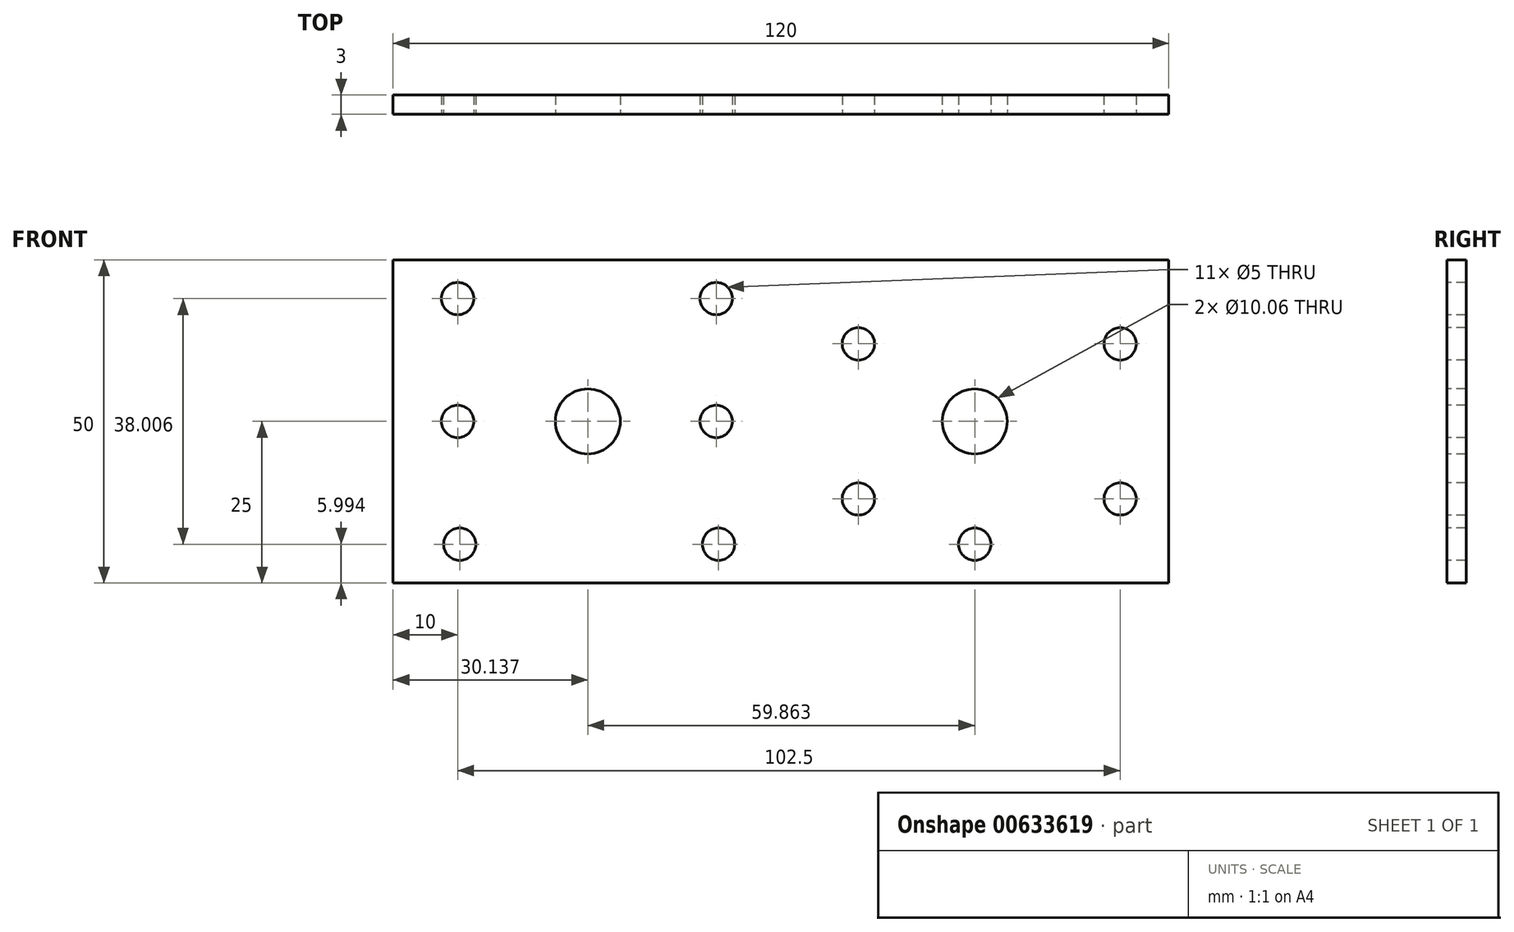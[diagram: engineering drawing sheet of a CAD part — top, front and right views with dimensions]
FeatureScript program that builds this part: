
annotation { "Feature Type Name" : "Feature", "Feature Type Description" : "" }
export const myFeature = defineFeature(function(context is Context, id is Id, definition is map)
    precondition{}
    {
        {
            var Q0;
            Q0=qCreatedBy(makeId("Front.planeOp"),FACE);
            var sketch = newSketch(context, id + "F0", { "sketchPlane" : qUnion([Q0])});
            skLineSegment(sketch, "E0.bottom", {"start": v(60, -25) * mm, "end": v(-60, -25) * mm});
            skLineSegment(sketch, "E0.top", {"start": v(60, 25) * mm, "end": v(-60, 25) * mm});
            skLineSegment(sketch, "E0.left", {"start": v(60, -25) * mm, "end": v(60, 25) * mm});
            skLineSegment(sketch, "E0.right", {"start": v(-60, -25) * mm, "end": v(-60, 25) * mm});
            skPoint(sketch, "E0.middle", {"position": v(0, 0) * mm});
            skSolve(sketch);
        }
        {
            var Q0;
            Q0 = qSketchRegion(id + "F0", true);
            extrude(context, id + "F1", {"entities" : qUnion([Q0]), "depth" : 3 * mm, "offsetDistance" : 25.4 * mm});
        }
        {
            var Q0;
            Q0=makeQuery(id+"F1.opExtrude","CAP_FACE",FACE,{"disambiguationData":[OSD([sQuery(id+"F0.wireOp",EDGE,"E0.bottom"),sQuery(id+"F0.wireOp",EDGE,"E0.top"),sQuery(id+"F0.wireOp",EDGE,"E0.left"),sQuery(id+"F0.wireOp",EDGE,"E0.right")])],"isStart":false});
            var sketch = newSketch(context, id + "F2", { "sketchPlane" : qUnion([Q0])});
            skCircle(sketch, "E1", {"center": v(-50, 19) * mm, "radius": 2.5 * mm});
            skLineSegment(sketch, "E2", {"start": v(-50, 19) * mm, "end": v(225.11, 19) * mm});
            skCircle(sketch, "E3", {"center": v(-10, 19) * mm, "radius": 2.5 * mm});
            skCircle(sketch, "E4", {"center": v(30, 19) * mm, "radius": 2.5 * mm});
            skCircle(sketch, "E5", {"center": v(-50, 0) * mm, "radius": 2.5 * mm});
            skPoint(sketch, "E5.centerSnap0", {"position": v(-60, 0) * mm});
            skCircle(sketch, "E6", {"center": v(-49.67, -19) * mm, "radius": 2.5 * mm});
            skCircle(sketch, "E7", {"center": v(-29.86, 0) * mm, "radius": 5.03 * mm});
            skCircle(sketch, "E8", {"center": v(-10, 0) * mm, "radius": 2.5 * mm});
            skCircle(sketch, "E9", {"center": v(-9.64, -19) * mm, "radius": 2.5 * mm});
            skCircle(sketch, "E10", {"center": v(12, 12) * mm, "radius": 2.5 * mm});
            skCircle(sketch, "E11", {"center": v(12, -12) * mm, "radius": 2.5 * mm});
            skCircle(sketch, "E12", {"center": v(30, 0) * mm, "radius": 5.03 * mm});
            skCircle(sketch, "E13", {"center": v(30, -19) * mm, "radius": 2.5 * mm});
            skCircle(sketch, "E14", {"center": v(52.5, 12) * mm, "radius": 2.5 * mm});
            skCircle(sketch, "E15", {"center": v(52.5, -12) * mm, "radius": 2.5 * mm});
            skSolve(sketch);
        }
        {
            var Q0;
            Q0=makeQuery(id+"F2.imprint","IMPRINT",FACE,{"disambiguationData":[TD([[makeQuery(id+"F2.imprint","IMPRINT",EDGE,{"derivedFrom":sQuery(id+"F2.wireOp",EDGE,"E5")}),1.0]])]});
            var Q1;
            Q1=makeQuery(id+"F2.imprint","IMPRINT",FACE,{"disambiguationData":[TD([[makeQuery(id+"F2.imprint","IMPRINT",EDGE,{"derivedFrom":sQuery(id+"F2.wireOp",EDGE,"E6")}),1.0]])]});
            var Q2;
            Q2=makeQuery(id+"F2.imprint","IMPRINT",FACE,{"disambiguationData":[TD([[makeQuery(id+"F2.imprint","IMPRINT",EDGE,{"derivedFrom":sQuery(id+"F2.wireOp",EDGE,"E7")}),1.0]])]});
            var Q3;
            Q3=makeQuery(id+"F2.imprint","IMPRINT",FACE,{"disambiguationData":[TD([[makeQuery(id+"F2.imprint","IMPRINT",EDGE,{"derivedFrom":sQuery(id+"F2.wireOp",EDGE,"E8")}),1.0]])]});
            var Q4;
            Q4=makeQuery(id+"F2.imprint","IMPRINT",FACE,{"disambiguationData":[TD([[makeQuery(id+"F2.imprint","IMPRINT",EDGE,{"derivedFrom":sQuery(id+"F2.wireOp",EDGE,"E9")}),1.0]])]});
            var Q5;
            Q5=makeQuery(id+"F2.imprint","IMPRINT",FACE,{"disambiguationData":[TD([[makeQuery(id+"F2.imprint","IMPRINT",EDGE,{"derivedFrom":sQuery(id+"F2.wireOp",EDGE,"E10")}),1.0]])]});
            var Q6;
            Q6=makeQuery(id+"F2.imprint","IMPRINT",FACE,{"disambiguationData":[TD([[makeQuery(id+"F2.imprint","IMPRINT",EDGE,{"derivedFrom":sQuery(id+"F2.wireOp",EDGE,"E11")}),1.0]])]});
            var Q7;
            Q7=makeQuery(id+"F2.imprint","IMPRINT",FACE,{"disambiguationData":[TD([[makeQuery(id+"F2.imprint","IMPRINT",EDGE,{"derivedFrom":sQuery(id+"F2.wireOp",EDGE,"E12")}),1.0]])]});
            var Q8;
            Q8=makeQuery(id+"F2.imprint","IMPRINT",FACE,{"disambiguationData":[TD([[makeQuery(id+"F2.imprint","IMPRINT",EDGE,{"derivedFrom":sQuery(id+"F2.wireOp",EDGE,"E13")}),1.0]])]});
            var Q9;
            Q9=makeQuery(id+"F2.imprint","IMPRINT",FACE,{"disambiguationData":[TD([[makeQuery(id+"F2.imprint","IMPRINT",EDGE,{"derivedFrom":sQuery(id+"F2.wireOp",EDGE,"E14")}),1.0]])]});
            var Q10;
            Q10=makeQuery(id+"F2.imprint","IMPRINT",FACE,{"disambiguationData":[TD([[makeQuery(id+"F2.imprint","IMPRINT",EDGE,{"derivedFrom":sQuery(id+"F2.wireOp",EDGE,"E15")}),1.0]])]});
            var Q11;
            {var subQ0=sQuery(id+"F2.wireOp",EDGE,"E3");var subQ1=sQuery(id+"F2.wireOp",EDGE,"E2");var subQ2=makeQuery(id+"F2.imprint","INTERSECT",VERTEX,{"disambiguationData":[OD(0.0)],"derivedFrom":[subQ1,subQ0]});Q11=makeQuery(id+"F2.imprint","IMPRINT",FACE,{"disambiguationData":[TD([[makeQuery(id+"F2.imprint","IMPRINT",EDGE,{"disambiguationData":[TD([[subQ2,-1.0]])],"derivedFrom":subQ1}),1.0]])]});}
            var Q12;
            {var subQ0=sQuery(id+"F2.wireOp",EDGE,"E3");var subQ1=sQuery(id+"F2.wireOp",EDGE,"E2");var subQ2=makeQuery(id+"F2.imprint","INTERSECT",VERTEX,{"disambiguationData":[OD(0.0)],"derivedFrom":[subQ1,subQ0]});Q12=makeQuery(id+"F2.imprint","IMPRINT",FACE,{"disambiguationData":[TD([[makeQuery(id+"F2.imprint","IMPRINT",EDGE,{"disambiguationData":[TD([[subQ2,-1.0]])],"derivedFrom":subQ1}),-1.0]])]});}
            var Q13;
            {var subQ0=sQuery(id+"F2.wireOp",EDGE,"E4");var subQ1=sQuery(id+"F2.wireOp",EDGE,"E2");var subQ2=makeQuery(id+"F2.imprint","INTERSECT",VERTEX,{"disambiguationData":[OD(0.0)],"derivedFrom":[subQ1,subQ0]});Q13=makeQuery(id+"F2.imprint","IMPRINT",FACE,{"disambiguationData":[TD([[makeQuery(id+"F2.imprint","IMPRINT",EDGE,{"disambiguationData":[TD([[subQ2,-1.0]])],"derivedFrom":subQ1}),1.0]])]});}
            var Q14;
            {var subQ0=sQuery(id+"F2.wireOp",EDGE,"E4");var subQ1=sQuery(id+"F2.wireOp",EDGE,"E2");var subQ2=makeQuery(id+"F2.imprint","INTERSECT",VERTEX,{"disambiguationData":[OD(0.0)],"derivedFrom":[subQ1,subQ0]});Q14=makeQuery(id+"F2.imprint","IMPRINT",FACE,{"disambiguationData":[TD([[makeQuery(id+"F2.imprint","IMPRINT",EDGE,{"disambiguationData":[TD([[subQ2,-1.0]])],"derivedFrom":subQ1}),-1.0]])]});}
            var Q15;
            Q15=makeQuery(id+"F2.imprint","IMPRINT",FACE,{"disambiguationData":[TD([[makeQuery(id+"F2.imprint","IMPRINT",EDGE,{"derivedFrom":sQuery(id+"F2.wireOp",EDGE,"E1")}),1.0]])]});
            extrude(context, id + "F3", {"entities" : qUnion([Q0, Q1, Q2, Q3, Q4, Q5, Q6, Q7, Q8, Q9, Q10, Q11, Q12, Q13, Q14, Q15]), "operationType" : NewBodyOperationType.REMOVE, "endBound" : BoundingType.THROUGH_ALL, "oppositeDirection" : true, "depth" : 25 * mm, "offsetDistance" : 25 * mm});
        }
    });
